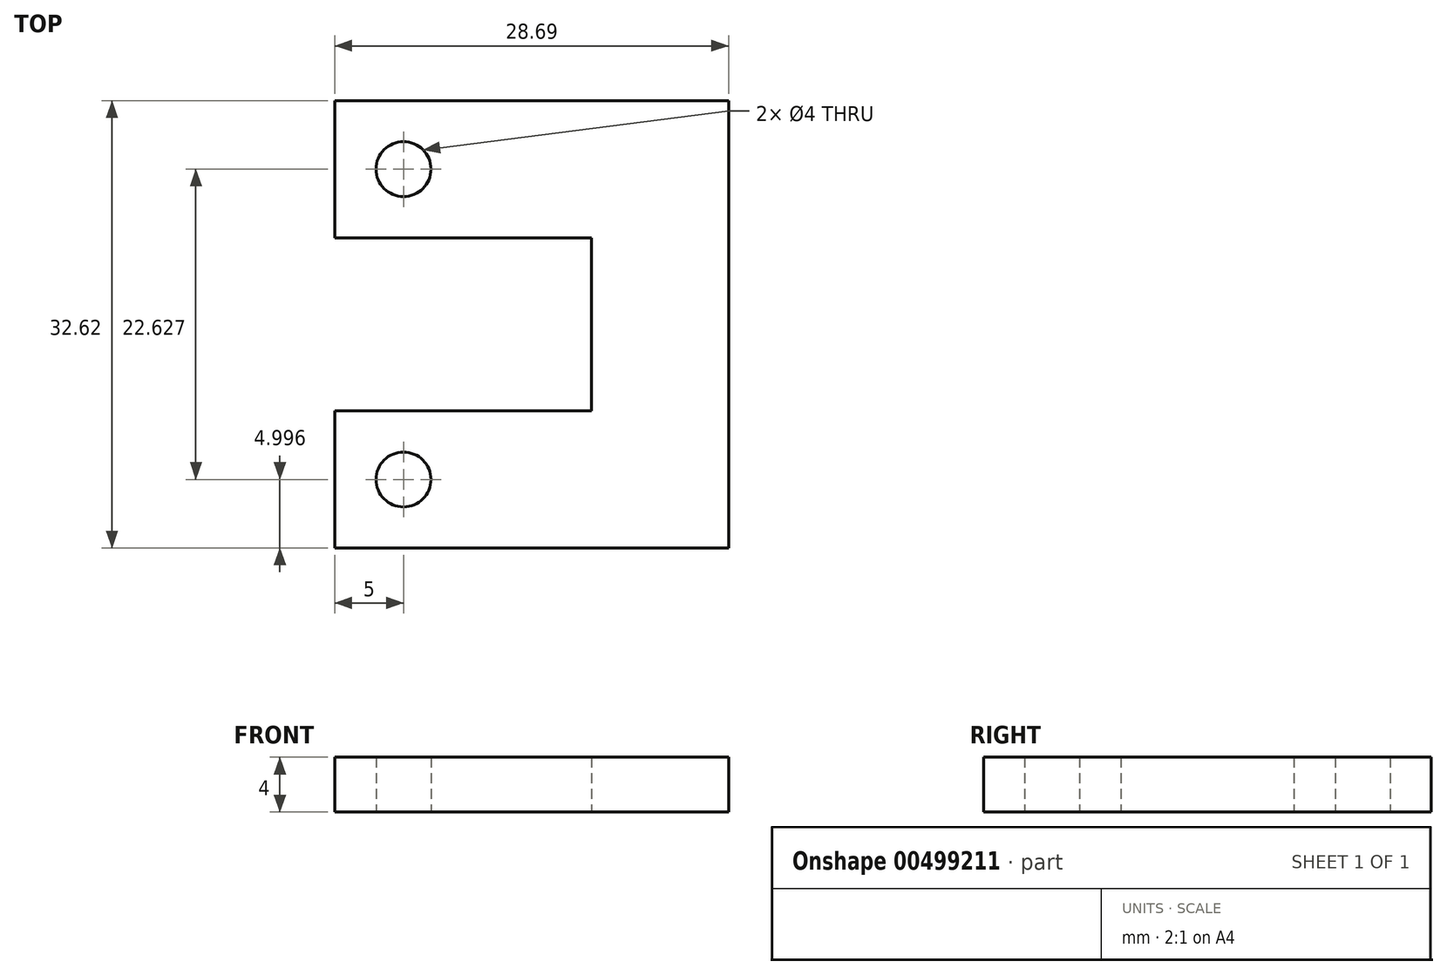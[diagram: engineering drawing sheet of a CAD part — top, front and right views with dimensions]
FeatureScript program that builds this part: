
annotation { "Feature Type Name" : "Feature", "Feature Type Description" : "" }
export const myFeature = defineFeature(function(context is Context, id is Id, definition is map)
    precondition{}
    {
        {
            var Q0;
            Q0=qCreatedBy(makeId("Top.planeOp"),FACE);
            var sketch = newSketch(context, id + "F0", { "sketchPlane" : qUnion([Q0])});
            skCircle(sketch, "E0", {"center": v(0, 11.31) * mm, "radius": 2 * mm});
            skCircle(sketch, "E1", {"center": v(0, -11.31) * mm, "radius": 2 * mm});
            skLineSegment(sketch, "E2.bottom", {"start": v(5, 16.31) * mm, "end": v(-5, 16.31) * mm});
            skLineSegment(sketch, "E2.top", {"start": v(5, 6.31) * mm, "end": v(-5, 6.31) * mm});
            skLineSegment(sketch, "E2.right", {"start": v(-5, 16.31) * mm, "end": v(-5, 6.31) * mm});
            skLineSegment(sketch, "E3.bottom", {"start": v(5, -6.31) * mm, "end": v(-5, -6.31) * mm});
            skLineSegment(sketch, "E3.top", {"start": v(5, -16.31) * mm, "end": v(-5, -16.31) * mm});
            skLineSegment(sketch, "E3.right", {"start": v(-5, -6.31) * mm, "end": v(-5, -16.31) * mm});
            skLineSegment(sketch, "E4", {"start": v(5, 16.31) * mm, "end": v(23.69, 16.31) * mm});
            skLineSegment(sketch, "E5", {"start": v(23.69, 16.31) * mm, "end": v(23.69, -16.31) * mm});
            skLineSegment(sketch, "E6", {"start": v(23.69, -16.31) * mm, "end": v(5, -16.31) * mm});
            skLineSegment(sketch, "E7", {"start": v(5, 6.31) * mm, "end": v(13.69, 6.31) * mm});
            skLineSegment(sketch, "E8", {"start": v(13.69, 6.31) * mm, "end": v(13.69, -6.31) * mm});
            skLineSegment(sketch, "E9", {"start": v(13.69, -6.31) * mm, "end": v(5, -6.31) * mm});
            skPoint(sketch, "E10", {"position": v(-11.31, 0) * mm});
            skSolve(sketch);
        }
        {
            var Q0;
            Q0 = qSketchRegion(id + "F0", true);
            extrude(context, id + "F1", {"entities" : qUnion([Q0]), "depth" : 4 * mm});
        }
    });
